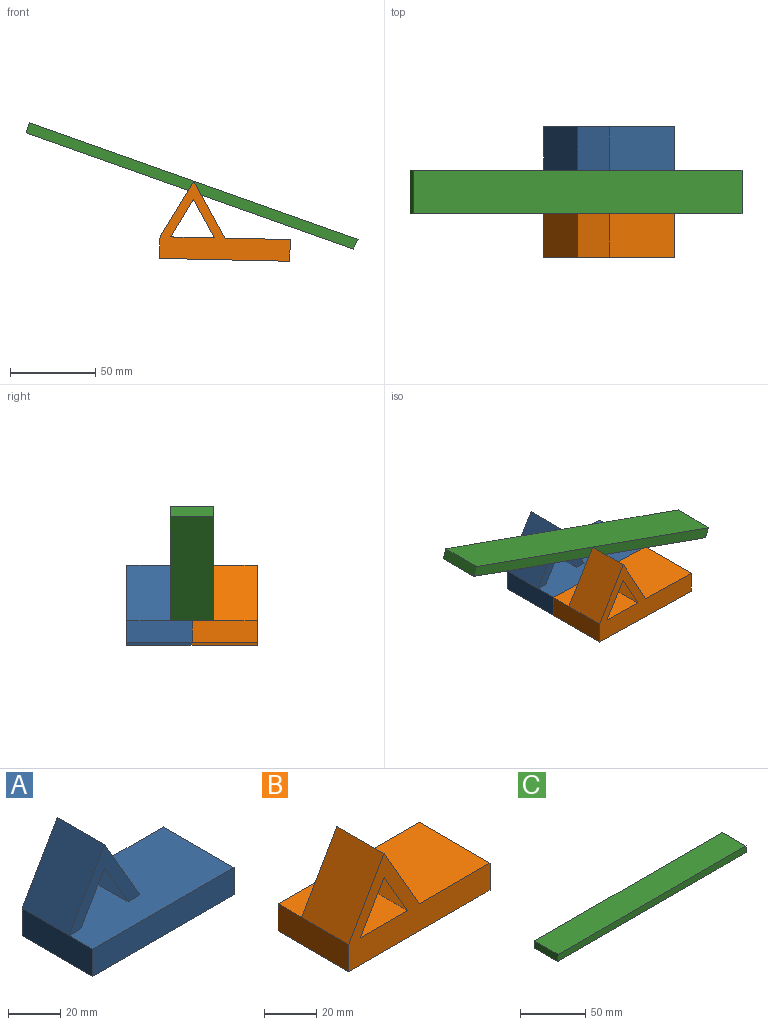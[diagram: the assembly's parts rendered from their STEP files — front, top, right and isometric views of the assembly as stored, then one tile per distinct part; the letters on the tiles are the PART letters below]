
ASSEMBLY  parts=3 mates=2
PART A: 11 faces, bbox 76.2x38.1x45.7 mm
  f0: plane 76.2x38.1mm, normal (0,0,1), area 2580.6mm2, adj f1,f3,f4,f5,f6,f7,f8,f10
  f1: plane 38.1x12.7mm, normal (-1,0,0), area 483.9mm2, adj f0,f2,f4,f5,f9
  f2: plane 76.2x38.1mm, normal (0,0,-1), area 2903.2mm2, adj f1,f3,f4,f5
  f3: plane 38.1x12.7mm, normal (1,0,0), area 483.9mm2, adj f0,f2,f4,f5
  f4: plane 76.2x12.7mm, normal (0,-1,0), area 967.7mm2, adj f0,f1,f2,f3
  f5: plane 76.2x45.7mm, normal (0,1,0), area 1316.9mm2, adj f0,f1,f2,f3,f6,f7,f8,f9
  f6: plane 25.4x22mm, normal (0.87,0,-0.5), area 645.2mm2, adj f0,f5,f7,f10
  f7: plane 25.4x22mm, normal (-0.87,0,-0.5), area 645.2mm2, adj f0,f5,f6,f10
  f8: plane 33x25.4mm, normal (0.87,0,0.5), area 967.7mm2, adj f0,f5,f9,f10
  f9: plane 33x25.4mm, normal (-0.87,0,0.5), area 967.7mm2, adj f1,f5,f8,f10
  f10: plane 38.1x33mm, normal (0,-1,0), area 349.2mm2, adj f0,f6,f7,f8,f9
PART B: 11 faces, bbox 76.2x38.1x45.7 mm
  f0: plane 76.2x38.1mm, normal (0,0,1), area 2580.6mm2, adj f1,f3,f4,f5,f6,f7,f8,f10
  f1: plane 38.1x12.7mm, normal (-1,0,0), area 483.9mm2, adj f0,f2,f4,f5,f9
  f2: plane 76.2x38.1mm, normal (0,0,-1), area 2903.2mm2, adj f1,f3,f4,f5
  f3: plane 38.1x12.7mm, normal (1,0,0), area 483.9mm2, adj f0,f2,f4,f5
  f4: plane 76.2x12.7mm, normal (0,1,0), area 967.7mm2, adj f0,f1,f2,f3
  f5: plane 76.2x45.7mm, normal (0,-1,0), area 1316.9mm2, adj f0,f1,f2,f3,f6,f7,f8,f9
  f6: plane 25.4x22mm, normal (0.87,0,-0.5), area 645.2mm2, adj f0,f5,f7,f10
  f7: plane 25.4x22mm, normal (-0.87,0,-0.5), area 645.2mm2, adj f0,f5,f6,f10
  f8: plane 33x25.4mm, normal (0.87,0,0.5), area 967.7mm2, adj f0,f5,f9,f10
  f9: plane 33x25.4mm, normal (-0.87,0,0.5), area 967.7mm2, adj f1,f5,f8,f10
  f10: plane 38.1x33mm, normal (0,1,0), area 349.2mm2, adj f0,f6,f7,f8,f9
PART C: 6 faces, bbox 203.9x25.4x6.4 mm
  f0: plane 203.2x25.4mm, normal (0,0,1), area 5161.3mm2, adj f1,f3,f4,f5
  f1: plane 25.4x6.35mm, normal (-0.99,0,0.1), area 162.2mm2, adj f0,f2,f4,f5
  f2: plane 203.86x25.4mm, normal (0,0,-1), area 5178.1mm2, adj f1,f3,f4,f5
  f3: plane 25.4x6.35mm, normal (1,0,0), area 161.3mm2, adj f0,f2,f4,f5
  f4: plane 203.86x6.35mm, normal (0,-1,0), area 1292.4mm2, adj f0,f1,f2,f3
  f5: plane 203.86x6.35mm, normal (0,1,0), area 1292.4mm2, adj f0,f1,f2,f3
PLACE A rot(axis=(0,1,0),1.2deg) t=(-23.79,21.76,54.61)mm
PLACE B rot(axis=(0,1,0),1.2deg) t=(-23.79,-54.44,54.61)mm
PLACE C rot(axis=(0,-1,0),160.5deg) t=(-56.35,-3.64,60.82)mm
MATE fastened B.f4 <-> A.f4  axis (0,1,0) through (-62.15,-16.34,42.74)mm
MATE ball C.f5 <-> A.f10  axis (0,1,0) through (-42.11,-3.64,88.01)mm
